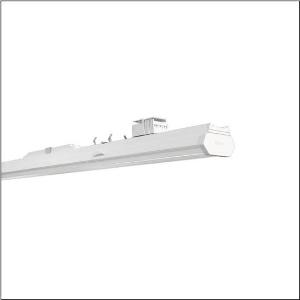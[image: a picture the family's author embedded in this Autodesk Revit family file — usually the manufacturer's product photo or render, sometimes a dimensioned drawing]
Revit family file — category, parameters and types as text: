
# Revit family: licross_21_protected_ho_52td12cn4cxm
name_source: partatom
category: Lighting Fixtures
units: mm (PartAtom-declared; Revit-internal decimal feet)

## family parameters
Cut with Voids When Loaded = No
Host = Face
Light Source = No
Part Type = Normal
Room Calculation Point = No
Round Connector Dimension = Use Diameter
Shared = No

## types (1)
- --- (1 x LED, 12460 lm, 68.9 W, 4000K)
    Apparent Load = 69 VA
    CIE Flux Codes = 70 91 97 98 100
    Color Rendering = 80
    Color Temperature = 4000K
    Default Elevation = 1800 mm
    Description = Licross 21 Protected HO, luminaire insert, of sheet steel, galvanised, coil coated, white, length: 1.500mm, width: 90mm, height: 103mm, LED rated luminous flux: 12.460lm, light colour: 840, SDCM (Standard Deviation of Colour Matching)MacAdam ≤ 3 SDCM (initial), control gear: ON/OFF Multilumen, CLOi, with plug, 3-pole, with phase selection, mains connection: 220..240V, AC, 50/60Hz, start of lifetime: 69W, end of service life: 83W, internal wiring halogen-free, primary light control with lens, of plastic, primary optical cover: cover, of PMMA, light emission: direct distribution, primary light characteristic: symmetric, protection rating (complete): IP54, insulation class (complete): insulation class I (protective earthing), certification: CE, ENEC, VDE, UKCA, protection symbol: D if used in an environment with non-conductive dust loads with corresponding accessories, impact resistance: IK06, permissible ambient temperature for indoor applications: -35..+35°C, corresponds to IFS (International Featured Standards) requirements for safety and quality in the food industry, reducing of maximum allowable ambient temperature of 5°C with ceiling mounting, LABS conformity tested according to VDMA 24364:2018-05, The light source and the operating device comply with the requirements of the Ecodesign Regulation (EU) 2019/2020 and are replaceable in accordance with this regulation, packaging unit: 1 piece
    Height = 92 mm
    Lamp = 1 x LED
    Lamp Light Flux = 12460 lm
    Lamp Power = 68.9 W
    Lamp count = 1
    Length = 1500 mm
    Luminous efficacy = 181 lm/W
    Manufacturer = Siteco
    ModVariant = No
    Model = 52TD12CN4CXM
    Mounting Place = Ceiling
    Mounting Type = Pendant
    Number of Poles = 1
    OnlyDefault = Yes
    Power Factor = 1
    Product Name = Licross 21 Protected HO
    Product group = luminaire insert | ceiling pendant
    ProductGroupID = 901
    Protection Class = Protection class I
    Protection Degree = IP 54
    RLX_Detail_Level = 1
    RLX_Emergency_Light_Flux = 0 lm
    RLX_Emergency_Type = 0
    RLX_Emergency_Type_DB = No
    RlxData = <blob elided: 22481 chars, md5=28094c8e>
    Socket = socket
    Standby Power = 0 W
    System Light Flux = 12460 lm
    System Power = 69 W
    Type Comments = factory setting: luminous flux: 100 % | (A | C | E) | 162 mA
    Type Image = l_1256148.jpg
    URL = http://relux.com
    VarID = @adj_113005
    Voltage = 0 V
    Weight = 0.00 kg
    Width = 88 mm

## geometry (parser evidence)
native form markers: Blend x4, Sweep x10
no freeform markers — native parametric forms only
